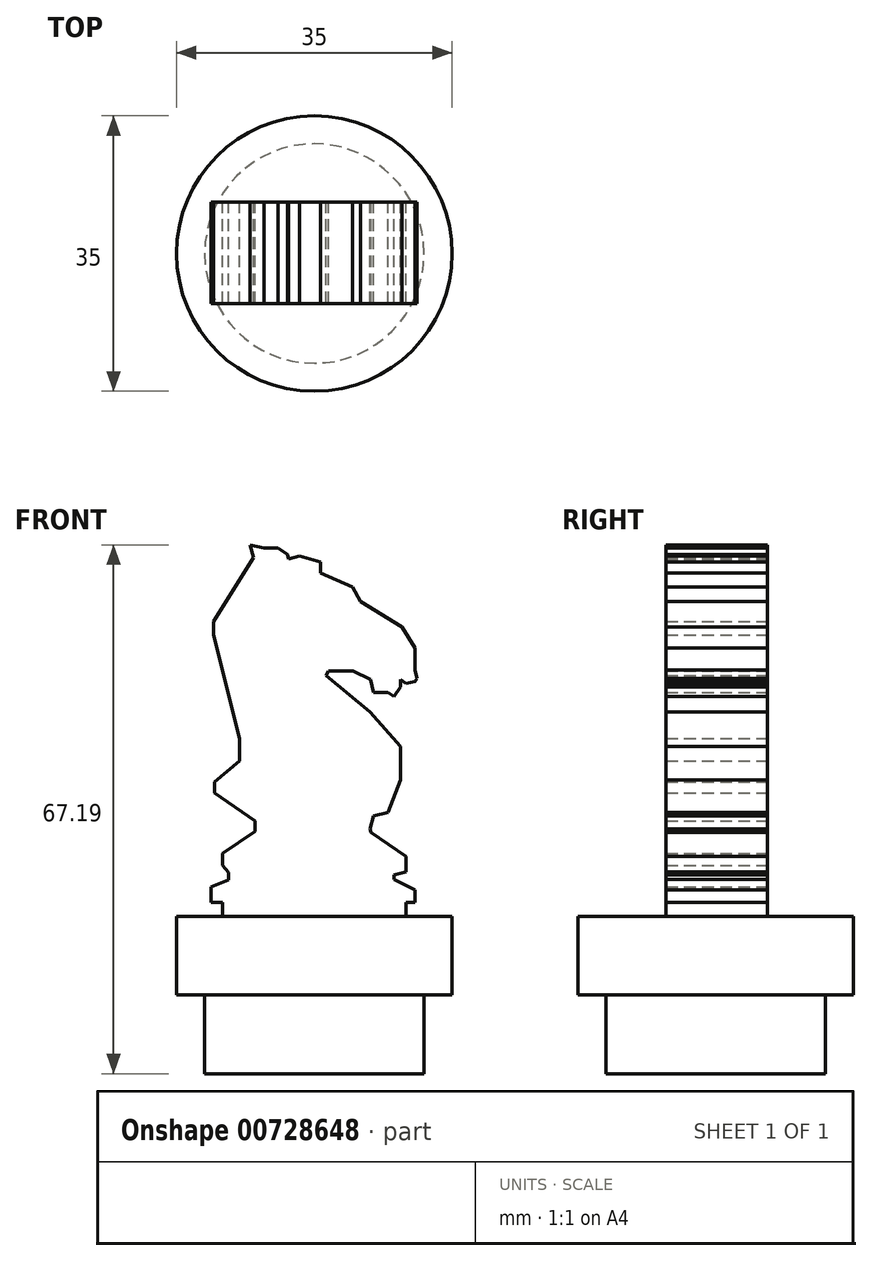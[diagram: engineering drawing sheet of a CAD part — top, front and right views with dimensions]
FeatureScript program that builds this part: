
annotation { "Feature Type Name" : "Feature", "Feature Type Description" : "" }
export const myFeature = defineFeature(function(context is Context, id is Id, definition is map)
    precondition{}
    {
        {
            var Q0;
            Q0=qCreatedBy(makeId("Front.planeOp"),FACE);
            var sketch = newSketch(context, id + "F0", { "sketchPlane" : qUnion([Q0])});
            skLineSegment(sketch, "E0", {"start": v(0, -11.11) * mm, "end": v(-13.5, -11.11) * mm});
            skLineSegment(sketch, "E1", {"start": v(-13.5, -11.11) * mm, "end": v(-13.5, -9.36) * mm});
            skLineSegment(sketch, "E2", {"start": v(-13.5, -9.36) * mm, "end": v(-14.93, -9.36) * mm});
            skLineSegment(sketch, "E3", {"start": v(-14.93, -9.36) * mm, "end": v(-14.93, -7.39) * mm});
            skLineSegment(sketch, "E4", {"start": v(-14.93, -7.39) * mm, "end": v(-12.7, -6.47) * mm});
            skLineSegment(sketch, "E5", {"start": v(-12.7, -6.47) * mm, "end": v(-12.7, -5.55) * mm});
            skLineSegment(sketch, "E6", {"start": v(-12.7, -5.55) * mm, "end": v(-13.5, -4.63) * mm});
            skLineSegment(sketch, "E7", {"start": v(-13.5, -4.63) * mm, "end": v(-13.5, -3.15) * mm});
            skLineSegment(sketch, "E8", {"start": v(-13.5, -3.15) * mm, "end": v(-9.38, -0.3) * mm});
            skLineSegment(sketch, "E9", {"start": v(-9.38, -0.3) * mm, "end": v(-9.38, 1) * mm});
            skLineSegment(sketch, "E10", {"start": v(-9.38, 1) * mm, "end": v(-14.54, 4.54) * mm});
            skLineSegment(sketch, "E11", {"start": v(-14.54, 4.54) * mm, "end": v(-14.54, 5.94) * mm});
            skLineSegment(sketch, "E12", {"start": v(-14.54, 5.94) * mm, "end": v(-11.35, 8.6) * mm});
            skLineSegment(sketch, "E13", {"start": v(-11.35, 8.6) * mm, "end": v(-11.35, 11.5) * mm});
            skLineSegment(sketch, "E14", {"start": v(-11.35, 11.5) * mm, "end": v(-14.23, 23) * mm});
            skLineSegment(sketch, "E15", {"start": v(-14.23, 23) * mm, "end": v(-14.65, 24.64) * mm});
            skLineSegment(sketch, "E16", {"start": v(-14.65, 24.64) * mm, "end": v(-14.65, 26.31) * mm});
            skLineSegment(sketch, "E17", {"start": v(-14.65, 26.31) * mm, "end": v(-9.56, 34.44) * mm});
            skLineSegment(sketch, "E18", {"start": v(-9.56, 34.44) * mm, "end": v(-9.97, 36.08) * mm});
            skLineSegment(sketch, "E19", {"start": v(-9.97, 36.08) * mm, "end": v(-8.2, 35.67) * mm});
            skLineSegment(sketch, "E20", {"start": v(-8.2, 35.67) * mm, "end": v(-6.45, 35.67) * mm});
            skLineSegment(sketch, "E21", {"start": v(-6.45, 35.67) * mm, "end": v(-5.25, 34.84) * mm});
            skLineSegment(sketch, "E22", {"start": v(-5.25, 34.84) * mm, "end": v(-5.12, 34.3) * mm});
            skLineSegment(sketch, "E23", {"start": v(-5.12, 34.3) * mm, "end": v(-3.74, 34.64) * mm});
            skLineSegment(sketch, "E24", {"start": v(-3.74, 34.64) * mm, "end": v(-1.03, 33.92) * mm});
            skLineSegment(sketch, "E25", {"start": v(-1.03, 33.92) * mm, "end": v(-1.03, 32.48) * mm});
            skLineSegment(sketch, "E26", {"start": v(-1.03, 32.48) * mm, "end": v(2.99, 30.68) * mm});
            skLineSegment(sketch, "E27", {"start": v(2.99, 30.68) * mm, "end": v(4.04, 28.85) * mm});
            skLineSegment(sketch, "E28", {"start": v(4.04, 28.85) * mm, "end": v(9.28, 25.66) * mm});
            skLineSegment(sketch, "E29", {"start": v(9.28, 25.66) * mm, "end": v(10.94, 23) * mm});
            skLineSegment(sketch, "E30", {"start": v(10.94, 23) * mm, "end": v(10.94, 21.77) * mm});
            skLineSegment(sketch, "E31", {"start": v(10.94, 21.77) * mm, "end": v(10.94, 21.16) * mm});
            skLineSegment(sketch, "E32", {"start": v(10.94, 21.16) * mm, "end": v(10.94, 20.2) * mm});
            skLineSegment(sketch, "E33", {"start": v(10.94, 20.2) * mm, "end": v(11.21, 19.12) * mm});
            skLineSegment(sketch, "E34", {"start": v(11.21, 19.12) * mm, "end": v(10.94, 18.73) * mm});
            skLineSegment(sketch, "E35", {"start": v(10.94, 18.73) * mm, "end": v(9.83, 18.45) * mm});
            skLineSegment(sketch, "E36", {"start": v(9.83, 18.45) * mm, "end": v(9.1, 18.96) * mm});
            skLineSegment(sketch, "E37", {"start": v(9.1, 18.96) * mm, "end": v(9.1, 18) * mm});
            skLineSegment(sketch, "E38", {"start": v(9.1, 18) * mm, "end": v(8.29, 16.83) * mm});
            skLineSegment(sketch, "E39", {"start": v(8.29, 16.83) * mm, "end": v(7.54, 17.34) * mm});
            skLineSegment(sketch, "E40", {"start": v(7.54, 17.34) * mm, "end": v(5.7, 17.34) * mm});
            skLineSegment(sketch, "E41", {"start": v(5.7, 17.34) * mm, "end": v(5.3, 18.96) * mm});
            skLineSegment(sketch, "E42", {"start": v(5.3, 18.96) * mm, "end": v(3.08, 20.02) * mm});
            skLineSegment(sketch, "E43", {"start": v(3.08, 20.02) * mm, "end": v(0, 20.02) * mm});
            skLineSegment(sketch, "E44", {"start": v(0, 20.02) * mm, "end": v(-0.37, 19.49) * mm});
            skLineSegment(sketch, "E45", {"start": v(-0.37, 19.49) * mm, "end": v(5.26, 14.86) * mm});
            skLineSegment(sketch, "E46", {"start": v(5.26, 14.86) * mm, "end": v(9.1, 10.45) * mm});
            skLineSegment(sketch, "E47", {"start": v(9.1, 10.45) * mm, "end": v(9.1, 6.21) * mm});
            skLineSegment(sketch, "E48", {"start": v(9.1, 6.21) * mm, "end": v(7.54, 2.09) * mm});
            skLineSegment(sketch, "E49", {"start": v(7.54, 2.09) * mm, "end": v(5.7, 1.62) * mm});
            skLineSegment(sketch, "E50", {"start": v(5.7, 1.62) * mm, "end": v(5.26, 0) * mm});
            skLineSegment(sketch, "E51", {"start": v(5.26, 0) * mm, "end": v(5.38, -0.48) * mm});
            skLineSegment(sketch, "E52", {"start": v(5.38, -0.48) * mm, "end": v(7.54, -1.96) * mm});
            skLineSegment(sketch, "E53", {"start": v(7.54, -1.96) * mm, "end": v(9.83, -3.53) * mm});
            skLineSegment(sketch, "E54", {"start": v(9.83, -3.53) * mm, "end": v(9.83, -5.46) * mm});
            skLineSegment(sketch, "E55", {"start": v(9.83, -5.46) * mm, "end": v(8.29, -5.84) * mm});
            skLineSegment(sketch, "E56", {"start": v(8.29, -5.84) * mm, "end": v(8.29, -6.43) * mm});
            skLineSegment(sketch, "E57", {"start": v(8.29, -6.43) * mm, "end": v(10.94, -7.74) * mm});
            skLineSegment(sketch, "E58", {"start": v(10.94, -7.74) * mm, "end": v(10.94, -9.36) * mm});
            skPoint(sketch, "E58.endSnap0", {"position": v(-14.21, -9.36) * mm});
            skLineSegment(sketch, "E59", {"start": v(10.94, -9.36) * mm, "end": v(9.83, -9.36) * mm});
            skLineSegment(sketch, "E60", {"start": v(9.83, -9.36) * mm, "end": v(9.83, -11.11) * mm});
            skLineSegment(sketch, "E61", {"start": v(9.83, -11.11) * mm, "end": v(0, -11.11) * mm});
            skSolve(sketch);
        }
        {
            var Q0;
            Q0=makeQuery(id+"F0.imprint","IMPRINT",FACE,{"disambiguationData":[TD([[makeQuery(id+"F0.imprint","IMPRINT",EDGE,{"derivedFrom":sQuery(id+"F0.wireOp",EDGE,"E0")}),-1.0]])]});
            extrude(context, id + "F1", {"entities" : qUnion([Q0]), "depth" : 12.9 * mm, "offsetDistance" : 25 * mm});
        }
        {
            var Q0;
            Q0=makeQuery(id+"F1.opExtrude","SWEPT_FACE",FACE,{"disambiguationData":[OSD([sQuery(id+"F0.wireOp",EDGE,"E0"),sQuery(id+"F0.wireOp",EDGE,"E61")])]});
            var sketch = newSketch(context, id + "F2", { "sketchPlane" : qUnion([Q0])});
            skCircle(sketch, "E62", {"center": v(-1.83, 6.56) * mm, "radius": 17.5 * mm});
            skPoint(sketch, "E62.centerSnap0", {"position": v(-1.83, 12.9) * mm});
            skSolve(sketch);
        }
        {
            var Q0;
            Q0 = qSketchRegion(id + "F2", true);
            extrude(context, id + "F3", {"entities" : qUnion([Q0]), "operationType" : NewBodyOperationType.ADD, "depth" : 10 * mm, "offsetDistance" : 25 * mm});
        }
        {
            var Q0;
            Q0=makeQuery(id+"F3.opExtrude","CAP_FACE",FACE,{"disambiguationData":[OSD([sQuery(id+"F2.wireOp",EDGE,"E62")])],"isStart":false});
            var sketch = newSketch(context, id + "F4", { "sketchPlane" : qUnion([Q0])});
            skCircle(sketch, "E63", {"center": v(-1.83, 6.56) * mm, "radius": 13.94 * mm});
            skSolve(sketch);
        }
        {
            var Q0;
            Q0=makeQuery(id+"F4.imprint","IMPRINT",FACE,{"disambiguationData":[TD([[makeQuery(id+"F4.imprint","IMPRINT",EDGE,{"derivedFrom":sQuery(id+"F4.wireOp",EDGE,"E63")}),1.0]])]});
            extrude(context, id + "F5", {"entities" : qUnion([Q0]), "operationType" : NewBodyOperationType.ADD, "depth" : 10 * mm, "offsetDistance" : 25 * mm});
        }
    });
